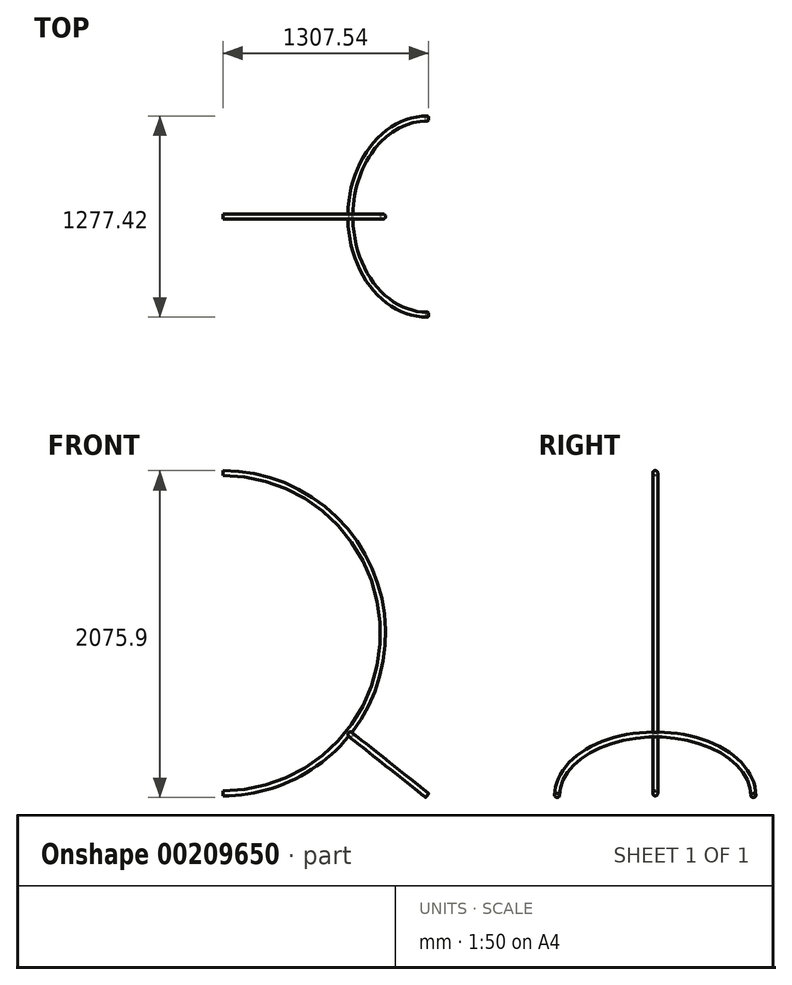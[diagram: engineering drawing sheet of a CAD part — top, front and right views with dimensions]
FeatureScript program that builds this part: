
annotation { "Feature Type Name" : "Feature", "Feature Type Description" : "" }
export const myFeature = defineFeature(function(context is Context, id is Id, definition is map)
    precondition{}
    {
        {
            var Q0;
            Q0=qCreatedBy(makeId("Front.planeOp"),FACE);
            var sketch = newSketch(context, id + "F0", { "sketchPlane" : qUnion([Q0])});
            skArc(sketch, "E0", {"start": v(-0.26, -1016) * mm, "mid": v(1016, 0) * mm, "end": v(-0.26, 1016) * mm});
            skLineSegment(sketch, "E1", {"start": v(-0.26, -1016) * mm, "end": v(-0.26, 1016) * mm, "construction": true});
            skSolve(sketch);
        }
        {
            var Q0;
            Q0=sQuery(id+"F0.wireOp",VERTEX,"E0.end");
            var Q1;
            Q1=qCreatedBy(makeId("Right.planeOp"),FACE);
            cPlane(context, id + "F1", {"entities" : qUnion([Q0, Q1]), "cplaneType" : CPlaneType.PLANE_POINT, "offset" : 25.4 * mm, "width" : 152.4 * mm, "height" : 152.4 * mm});
        }
        {
            var Q0;
            Q0=qCreatedBy(id+"F1.planeOp",FACE);
            var sketch = newSketch(context, id + "F2", { "sketchPlane" : qUnion([Q0])});
            skCircle(sketch, "E2", {"center": v(0, 1017.12) * mm, "radius": 15.88 * mm});
            skSolve(sketch);
        }
        {
            var Q0;
            Q0=makeQuery(id+"F2.imprint","IMPRINT",FACE,{"disambiguationData":[TD([[makeQuery(id+"F2.imprint","IMPRINT",EDGE,{"derivedFrom":sQuery(id+"F2.wireOp",EDGE,"E2")}),1.0]])]});
            var Q1;
            Q1=sQuery(id+"F0.wireOp",EDGE,"E0");
            sweep(context, id + "F3", {"profiles" : qUnion([Q0]), "path" : qUnion([Q1])});
        }
        {
            var Q0;
            Q0=qCreatedBy(makeId("Front.planeOp"),FACE);
            var sketch = newSketch(context, id + "F4", { "sketchPlane" : qUnion([Q0])});
            skLineSegment(sketch, "E3", {"start": v(0, 0) * mm, "end": v(1296.7, -1029.91) * mm, "construction": true});
            skLineSegment(sketch, "E4", {"start": v(1296.7, -1029.91) * mm, "end": v(0, -1029.91) * mm});
            skSolve(sketch);
        }
        {
            var Q0;
            Q0=sQuery(id+"F4.wireOp",EDGE,"E3");
            var Q1;
            Q1=qCreatedBy(makeId("Right.planeOp"),FACE);
            cPlane(context, id + "F5", {"entities" : qUnion([Q0, Q1]), "cplaneType" : CPlaneType.LINE_ANGLE, "offset" : 25.4 * mm, "angle" : 0 * degree, "width" : 152.4 * mm, "height" : 152.4 * mm});
        }
        {
            var Q0;
            Q0=qCreatedBy(id+"F5.planeOp",FACE);
            var sketch = newSketch(context, id + "F6", { "sketchPlane" : qUnion([Q0])});
            skPoint(sketch, "E5", {"position": v(1034.08, 0) * mm});
            skArc(sketch, "E6", {"start": v(1656.65, 622.57) * mm, "mid": v(1034.08, 0) * mm, "end": v(1656.65, -622.57) * mm});
            skSolve(sketch);
        }
        {
            var Q0;
            Q0=qCreatedBy(id+"F5.planeOp",FACE);
            var sketch = newSketch(context, id + "F7", { "sketchPlane" : qUnion([Q0])});
            skLineSegment(sketch, "E7", {"start": v(1656.85, 622.56) * mm, "end": v(1656.85, -622.52) * mm, "construction": true});
            skSolve(sketch);
        }
        {
            var Q0;
            Q0=sQuery(id+"F6.wireOp",VERTEX,"E6.end");
            var Q1;
            Q1=sQuery(id+"F7.wireOp",EDGE,"E7");
            cPlane(context, id + "F8", {"entities" : qUnion([Q0, Q1]), "cplaneType" : CPlaneType.LINE_ANGLE, "offset" : 25.4 * mm, "angle" : 90 * degree, "width" : 152.4 * mm, "height" : 152.4 * mm});
        }
        {
            var Q0;
            Q0=qCreatedBy(id+"F8.planeOp",FACE);
            var sketch = newSketch(context, id + "F9", { "sketchPlane" : qUnion([Q0])});
            skCircle(sketch, "E8", {"center": v(622.84, 0) * mm, "radius": 15.88 * mm});
            skSolve(sketch);
        }
        {
            var Q0;
            Q0=makeQuery(id+"F9.imprint","IMPRINT",FACE,{"disambiguationData":[TD([[makeQuery(id+"F9.imprint","IMPRINT",EDGE,{"derivedFrom":sQuery(id+"F9.wireOp",EDGE,"E8")}),1.0]])]});
            var Q1;
            Q1=sQuery(id+"F6.wireOp",EDGE,"E6");
            sweep(context, id + "F10", {"operationType" : NewBodyOperationType.ADD, "profiles" : qUnion([Q0]), "path" : qUnion([Q1])});
        }
    });
